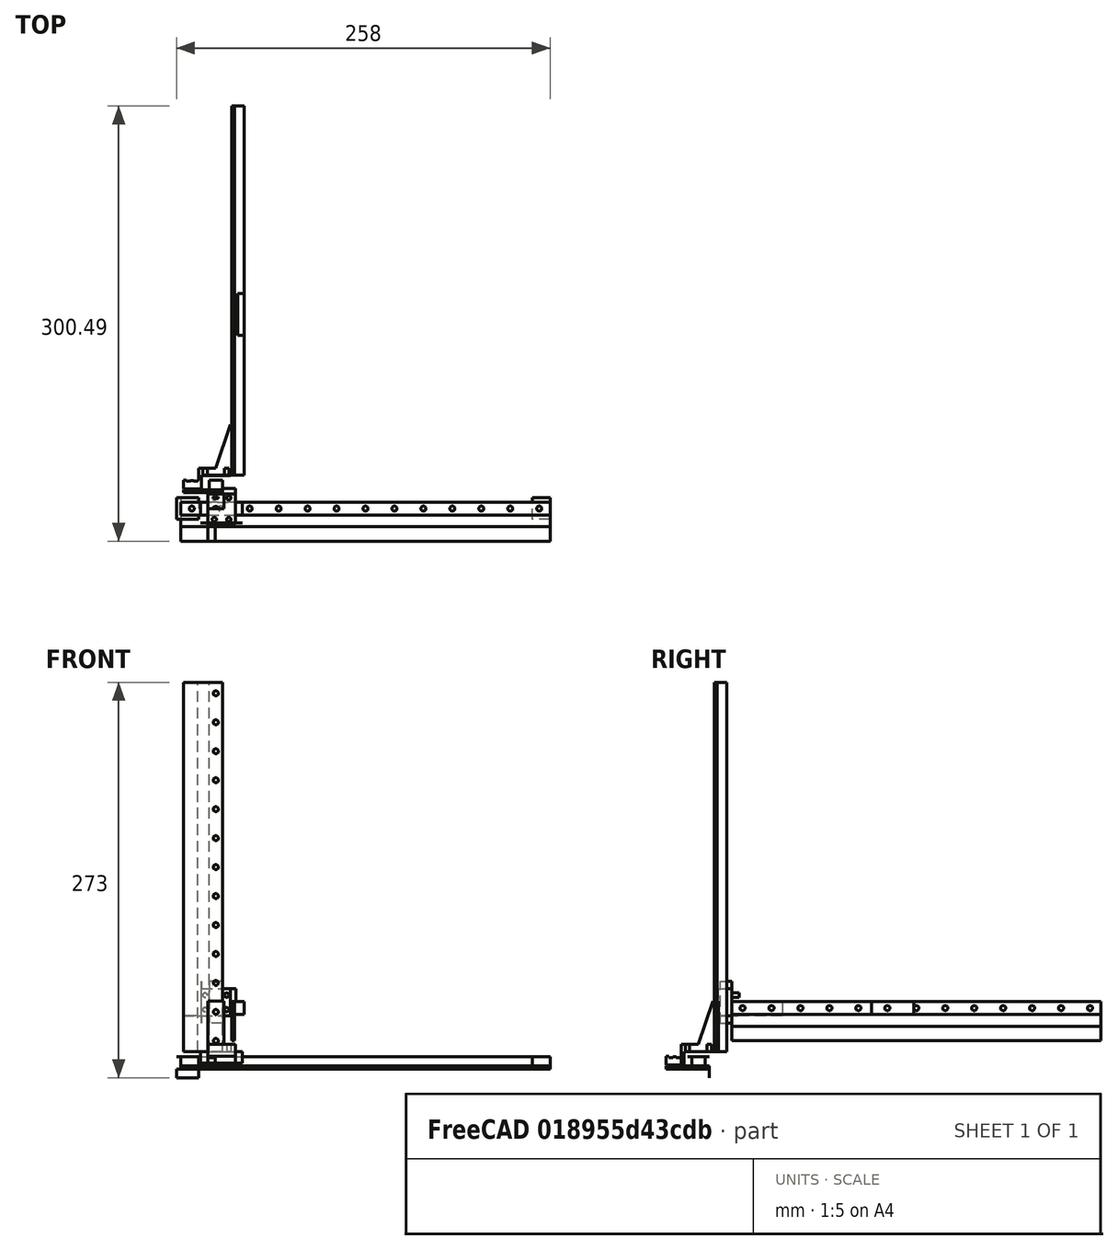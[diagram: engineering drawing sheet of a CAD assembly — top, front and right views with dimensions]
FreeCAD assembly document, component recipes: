
FREECAD ASSEMBLY — COMPONENT RECIPES ("v7")

This assembly document has 14 components, labeled P0..P13 below (a component is one placed body or linked part). 11 of them carry a construction recipe — the FreeCAD feature program that regenerates the part from scratch, quoted from this document or its linked companion documents; the rest are supplied as boundary geometry only. No exploded tour is included for this assembly.
COMPONENT P0 — recipe-attached ("Base_PCBLB", a linked part whose construction recipe lives in a companion FreeCAD document of the same project; that document's serialized recipe follows).
Construction recipe (the companion document, serialized — sketch geometry with constraints, then the solid features built on it; lengths are millimeters unless a unit is written):

FCSTD DOCUMENT  (FreeCAD 0.21R33668 +26 (Git))
Label: Base
License: All rights reserved
LicenseURL: http://en.wikipedia.org/wiki/All_rights_reserved
objects: Sketcher::SketchObject×4, PartDesign::Pad×3, PartDesign::SubShapeBinder×2, PartDesign::Pocket×1, PartDesign::Body×1
note: 15 computed .brp shape members not serialized (recipe doc carries the construction recipe); baked Part::Feature solids carry a one-line shape summary decoded from their .brp
EXTERNAL_REF file=MG/mgn9c_13.FCStd obj=Body
EXTERNAL_REF file=MG/mgn9c_slide.FCStd obj=Body001
EXTERNAL_REF file=MG/Datasheet.FCStd obj=Spreadsheet

FEATURE [PartDesign::SubShapeBinder] Binder  label="Rail"
  BindCopyOnChange = 0
  BindMode = 0
  ClaimChildren = false
  Context = -> Body [Binder.]
  Fuse = false
  MakeFace = true
  OffsetFill = false
  OffsetIntersection = false
  OffsetJoinType = 0
  OffsetOpenResult = false
  PartialLoad = false
  Relative = true
  Support = -> [<external MG/mgn9c_13.FCStd>#Body[LinearPattern.]]
  _Version = 2
FEATURE [PartDesign::SubShapeBinder] Binder001  label="Slide"
  BindCopyOnChange = 0
  BindMode = 0
  ClaimChildren = false
  Context = -> Body [Binder001.]
  Fuse = false
  MakeFace = true
  OffsetFill = false
  OffsetIntersection = false
  OffsetJoinType = 0
  OffsetOpenResult = false
  PartialLoad = false
  Placement = pos=(12,-5.5,2) rot=(0,0,1;0rad)
  Relative = true
  Support = -> [<external MG/mgn9c_slide.FCStd>#Body001]
  _Version = 2
FEATURE [Sketcher::SketchObject] Sketch
  ExternalGeometry = -> [Binder]
  FullyConstrained = true
  MapMode = 5
  Support = -> [XY_Plane]
  expr: Constraints[22] = .Constraints.Strength
  expr: Constraints[30] = .Constraints.Strength
  sketch-geometry (13):
    g0: LineSegment StartX=0 StartY=9 StartZ=0 EndX=12.25 EndY=9 EndZ=0
    g1: LineSegment StartX=12.25 StartY=0 StartZ=0 EndX=0 EndY=0 EndZ=0
    g2: LineSegment StartX=0 StartY=0 StartZ=0 EndX=0 EndY=9 EndZ=0
    g3: LineSegment StartX=12.25 StartY=-3 StartZ=0 EndX=-3 EndY=-3 EndZ=0
    g4: LineSegment StartX=-3 StartY=-3 StartZ=0 EndX=-3 EndY=12 EndZ=0
    g5: LineSegment StartX=-3 StartY=12 StartZ=0 EndX=12.25 EndY=12 EndZ=0
    g6: LineSegment StartX=12.25 StartY=12 StartZ=0 EndX=12.25 EndY=-3 EndZ=0
    g7: LineSegment StartX=12.25 StartY=12 StartZ=0 EndX=12.25 EndY=9 EndZ=0
    g8: LineSegment StartX=12.25 StartY=-3 StartZ=0 EndX=12.25 EndY=0 EndZ=0
    g9: GeomPoint X=12.25 Y=4.5 Z=0
    g10: LineSegment StartX=0 StartY=4.5 StartZ=0 EndX=12.25 EndY=4.5 EndZ=0
    g11: GeomPoint X=9.25 Y=4.5 Z=0
    g12: LineSegment StartX=0 StartY=0 StartZ=0 EndX=12.25 EndY=0 EndZ=0
  constraints (34):
    c: Coincident(g1,g2)
    c: Coincident(g2,g0)
    c: Horizontal(g0)
    c: Horizontal(g1)
    c: Vertical(g2)
    c: Coincident(g0,g-3)
    c: PointOnObject(g1,g-4)
    c: Coincident(g3,g4)
    c: Coincident(g4,g5)
    c: Coincident(g5,g6)
    c: Coincident(g6,g3)
    c: Horizontal(g3)
    c: Horizontal(g5)
    c: Vertical(g4)
    c: Vertical(g6)
    c: PointOnObject(g0,g6)
    c: Coincident(g7,g5)
    c: Coincident(g7,g0)
    c: Coincident(g8,g3)
    c: Coincident(g8,g1)
    c: Vertical(g8)
    c: DistanceY(g8,g8) = 3  'Strength'
    c: DistanceX(g3,g1) = 3
    c: PointOnObject(g9,g6)
    c: PointOnObject(g10,g2)
    c: Coincident(g10,g9)
    c: PointOnObject(g-5,g10)
    c: Symmetric(g3,g5,g10)
    c: PointOnObject(g11,g-5)
    c: PointOnObject(g11,g10)
    c: DistanceX(g11,g9) = 3
    c: Coincident(g12,g2)
    c: Coincident(g12,g8)
    c: DistanceX(g0,g0) = 12.25  'RailOverlap'
FEATURE [PartDesign::Pad] Pad
  Direction = (0,0,1)
  Length = 6.5
  Length2 = 10
  Profile = -> Sketch
  ReferenceAxis = -> Sketch [N_Axis]
  Type = 0
  expr: Length = <<Datasheet>>#<<mgn9c>>.Dim_Hr
FEATURE [Sketcher::SketchObject] Sketch001
  ExternalGeometry = -> [Pad]
  FullyConstrained = true
  MapMode = 5
  Placement = pos=(-3,0,0) rot=(0.57735,-0.57735,-0.57735;2.0944rad)
  Support = -> [Pad]
  sketch-geometry (4):
    g0: LineSegment StartX=-12 StartY=0 StartZ=0 EndX=3 EndY=0 EndZ=0
    g1: LineSegment StartX=3 StartY=0 StartZ=0 EndX=3 EndY=-2 EndZ=0
    g2: LineSegment StartX=3 StartY=-2 StartZ=0 EndX=-12 EndY=-2 EndZ=0
    g3: LineSegment StartX=-12 StartY=-2 StartZ=0 EndX=-12 EndY=0 EndZ=0
  constraints (10):
    c: Coincident(g0,g1)
    c: Coincident(g1,g2)
    c: Coincident(g2,g3)
    c: Coincident(g3,g0)
    c: Horizontal(g2)
    c: Vertical(g1)
    c: Vertical(g3)
    c: Coincident(g0,g-4)
    c: Coincident(g0,g-4)
    c: DistanceY(g1,g1) = 2  'PCB_Thickness'
FEATURE [PartDesign::Pad] Pad001
  BaseFeature = -> Pad
  Direction = (-1,0,0)
  Length = 3
  Length2 = 10
  Profile = -> Sketch001
  ReferenceAxis = -> Sketch001 [N_Axis]
  Reversed = true
  Type = 0
  expr: Length = <<Sketch>>.Constraints.Strength
FEATURE [Sketcher::SketchObject] Sketch002
  ExternalGeometry = -> [Pad001,Binder]
  FullyConstrained = true
  MapMode = 5
  Placement = pos=(0,0,-2) rot=(1,0,0;3.14159rad)
  Support = -> [Pad001]
  sketch-geometry (5):
    g0: LineSegment StartX=-3 StartY=-12 StartZ=0 EndX=12.25 EndY=-12 EndZ=0
    g1: LineSegment StartX=12.25 StartY=-12 StartZ=0 EndX=12.25 EndY=3 EndZ=0
    g2: LineSegment StartX=12.25 StartY=3 StartZ=0 EndX=-3 EndY=3 EndZ=0
    g3: LineSegment StartX=-3 StartY=3 StartZ=0 EndX=-3 EndY=-12 EndZ=0
    g4: Circle CenterX=7.5 CenterY=-4.5 CenterZ=0 NormalX=0 NormalY=0 NormalZ=1 AngleXU=0 Radius=1.75
  constraints (12):
    c: Coincident(g0,g1)
    c: Coincident(g1,g2)
    c: Coincident(g2,g3)
    c: Coincident(g3,g0)
    c: Horizontal(g0)
    c: Horizontal(g2)
    c: Vertical(g1)
    c: Vertical(g3)
    c: Coincident(g0,g-5)
    c: Coincident(g1,g-4)
    c: Coincident(g4,g-7)
    c: PointOnObject(g-6,g4)
FEATURE [PartDesign::Pad] Pad002
  BaseFeature = -> Pad001
  Direction = (0,0,-1)
  Length = 6
  Length2 = 10
  Profile = -> Sketch002
  ReferenceAxis = -> Sketch002 [N_Axis]
  Type = 0
  expr: Length = 6
FEATURE [Sketcher::SketchObject] Sketch003
  ExternalGeometry = -> [Pad002]
  FullyConstrained = true
  MapMode = 5
  Placement = pos=(0,0,-8) rot=(1,0,0;3.14159rad)
  Support = -> [Pad002]
  expr: Constraints[1] = <<Datasheet>>#<<mgn9c>>.Dim_D
  sketch-geometry (1):
    g0: Circle CenterX=7.5 CenterY=-4.5 CenterZ=0 NormalX=0 NormalY=0 NormalZ=1 AngleXU=0 Radius=3
  constraints (2):
    c: Coincident(g0,g-3)
    c: Diameter(g0) = 6
FEATURE [PartDesign::Pocket] Pocket
  BaseFeature = -> Pad002
  Direction = (0,0,1)
  Length = 5
  Length2 = 5
  Profile = -> Sketch003
  ReferenceAxis = -> Sketch003 [N_Axis]
  Type = 0
FEATURE [PartDesign::Body] Body  label="Base_PCB"
  Group = -> [Sketch,Binder001,Binder,Pad,Sketch001,Pad001,Sketch002,Pad002,Sketch003,Pocket]
  Origin = -> Origin
  Tip = -> Pocket
COMPONENT P1 — recipe-attached ("PCB", a linked part whose construction recipe lives in a companion FreeCAD document of the same project; that document's serialized recipe follows).
Construction recipe (the companion document, serialized — sketch geometry with constraints, then the solid features built on it; lengths are millimeters unless a unit is written):

FCSTD DOCUMENT  (FreeCAD 0.21R33668 +26 (Git))
Label: PCB_Linear_Potentiometer
License: All rights reserved
LicenseURL: http://en.wikipedia.org/wiki/All_rights_reserved
objects: Sketcher::SketchObject×3, PartDesign::SubShapeBinder×2, PartDesign::Pad×2, PartDesign::Pocket×1, PartDesign::LinearPattern×1, PartDesign::Body×1
note: 13 computed .brp shape members not serialized (recipe doc carries the construction recipe); baked Part::Feature solids carry a one-line shape summary decoded from their .brp
EXTERNAL_REF file=MG/mgn9c_13.FCStd obj=Body
EXTERNAL_REF file=MG/mgn9c_slide.FCStd obj=Body001
EXTERNAL_REF file=MG/Datasheet.FCStd obj=Spreadsheet
EXTERNAL_REF file=NormalConnector.FCStd obj=Sketch
EXTERNAL_REF file=Base.FCStd obj=Sketch001
EXTERNAL_REF file=Base.FCStd obj=Sketch

FEATURE [PartDesign::SubShapeBinder] Binder  label="Rail"
  BindCopyOnChange = 0
  BindMode = 0
  ClaimChildren = false
  Context = -> Body [Binder.]
  Fuse = false
  MakeFace = true
  OffsetFill = false
  OffsetIntersection = false
  OffsetJoinType = 0
  OffsetOpenResult = false
  PartialLoad = false
  Relative = true
  Support = -> [<external MG/mgn9c_13.FCStd>#Body]
  _Version = 2
FEATURE [PartDesign::SubShapeBinder] Binder001  label="Slide"
  BindCopyOnChange = 0
  BindMode = 0
  ClaimChildren = false
  Context = -> Body [Binder001.]
  Fuse = false
  MakeFace = true
  OffsetFill = false
  OffsetIntersection = false
  OffsetJoinType = 0
  OffsetOpenResult = false
  PartialLoad = false
  Placement = pos=(0,-5.5,0) rot=(0,0,1;0rad)
  Relative = true
  Support = -> [<external MG/mgn9c_slide.FCStd>#Body001]
  _Version = 2
FEATURE [Sketcher::SketchObject] Sketch
  ExternalGeometry = -> [Binder]
  FullyConstrained = true
  MapMode = 5
  Support = -> [XY_Plane]
  expr: Constraints[21] = <<Datasheet>>#<<mgn9c>>.Dim_W
  expr: Constraints[22] = NormalConnector#Sketch.Constraints.PCB_Edge_Distance_From_Slide_Side
  sketch-geometry (11):
    g0: LineSegment StartX=0 StartY=9 StartZ=0 EndX=255 EndY=9 EndZ=0
    g1: LineSegment StartX=255 StartY=9 StartZ=0 EndX=255 EndY=-17.9944 EndZ=0
    g2: LineSegment StartX=255 StartY=-17.9944 StartZ=0 EndX=0 EndY=-17.9944 EndZ=0
    g3: LineSegment StartX=0 StartY=-17.9944 StartZ=0 EndX=0 EndY=9 EndZ=0
    g4: LineSegment StartX=7.5 StartY=4.5 StartZ=0 EndX=27.5 EndY=4.5 EndZ=0
    g5: LineSegment StartX=7.5 StartY=14.5 StartZ=0 EndX=27.5 EndY=14.5 EndZ=0
    g6: LineSegment StartX=27.5 StartY=14.5 StartZ=0 EndX=27.5 EndY=-5.5 EndZ=0
    g7: LineSegment StartX=27.5 StartY=-5.5 StartZ=0 EndX=7.5 EndY=-5.5 EndZ=0
    g8: LineSegment StartX=7.5 StartY=-5.5 StartZ=0 EndX=7.5 EndY=14.5 EndZ=0
    g9: Circle CenterX=7.5 CenterY=4.5 CenterZ=0 NormalX=0 NormalY=0 NormalZ=1 AngleXU=0 Radius=1.75
    g10: GeomPoint X=9.25 Y=4.5 Z=0
  constraints (29):
    c: Coincident(g0,g1)
    c: Coincident(g1,g2)
    c: Coincident(g2,g3)
    c: Coincident(g3,g0)
    c: Horizontal(g2)
    c: Vertical(g1)
    c: Vertical(g3)
    c: Coincident(g0,g-3)
    c: Coincident(g0,g-4)
    c: Coincident(g4,g-5)
    c: Coincident(g4,g-6)
    c: Coincident(g5,g6)
    c: Coincident(g6,g7)
    c: Coincident(g7,g8)
    c: Coincident(g8,g5)
    c: Horizontal(g5)
    c: Horizontal(g7)
    c: Vertical(g6)
    c: PointOnObject(g4,g6)
    c: PointOnObject(g4,g8)
    c: Symmetric(g5,g7,g4)
    c: DistanceY(g8,g8) = 20
    c: DistanceY(g2,g7) = 12.4944
    c: Coincident(g9,g4)
    c: PointOnObject(g10,g4)
    c: PointOnObject(g10,g-5)
    c: PointOnObject(g10,g9)
    c: DistanceX(g0,g0) = 255  'Length'
    c: DistanceY(g1,g1) = 26.9944
FEATURE [PartDesign::Pad] Pad
  Direction = (0,0,1)
  Length = 2
  Length2 = 10
  Profile = -> Sketch
  ReferenceAxis = -> Sketch [N_Axis]
  Type = 0
  expr: Length = <<Base>>#<<Sketch001>>.Constraints.PCB_Thickness
FEATURE [Sketcher::SketchObject] Sketch001
  ExternalGeometry = -> [Pad]
  FullyConstrained = true
  MapMode = 5
  Placement = pos=(0,0,2) rot=(0,0,1;0rad)
  Support = -> [Pad]
  sketch-geometry (2):
    g0: Circle CenterX=7.5 CenterY=4.5 CenterZ=0 NormalX=0 NormalY=0 NormalZ=1 AngleXU=0 Radius=1.75
    g1: GeomPoint X=9.25 Y=4.5 Z=0
  constraints (4):
    c: PointOnObject(g1,g0)
    c: PointOnObject(g1,g-3)
    c: Coincident(g0,g-3)
    c: DistanceY(g1,g0) = 0
FEATURE [PartDesign::Pocket] Pocket
  BaseFeature = -> Pad
  Direction = (0,0,-1)
  Length = 5
  Length2 = 5
  Profile = -> Sketch001
  ReferenceAxis = -> Sketch001 [N_Axis]
  Type = 1
FEATURE [PartDesign::LinearPattern] LinearPattern
  BaseFeature = -> Pocket
  Direction = -> Sketch001 [H_Axis]
  Length = 240
  Occurrences = 13
  Originals = -> [Pocket]
  expr: Length = <<Sketch>>.Constraints.Length - <<Datasheet>>#<<mgn9c>>.Dim_E * 2
FEATURE [Sketcher::SketchObject] Sketch002
  ExternalGeometry = -> [LinearPattern]
  FullyConstrained = true
  MapMode = 5
  Placement = pos=(0,0,2) rot=(0,0,1;0rad)
  Support = -> [LinearPattern]
  expr: Constraints[18] = <<Datasheet>>#<<mgn9c>>.Dim_W / 2
  expr: Constraints[21] = NormalConnector#Sketch.Constraints.Connector_Close_Distance
  expr: Constraints[22] = NormalConnector#Sketch.Constraints.Connector_Far_Distance
  expr: Constraints[24] = .Constraints.Resistor_Width
  expr: Constraints[26] = <<Base>>#<<Sketch>>.Constraints.RailOverlap
  sketch-geometry (15):
    g0: LineSegment StartX=12.25 StartY=-7.4986 StartZ=0 EndX=242.75 EndY=-7.4986 EndZ=0
    g1: LineSegment StartX=242.75 StartY=-7.4986 StartZ=0 EndX=242.75 EndY=-11.4986 EndZ=0
    g2: LineSegment StartX=242.75 StartY=-11.4986 StartZ=0 EndX=12.25 EndY=-11.4986 EndZ=0
    g3: LineSegment StartX=12.25 StartY=-11.4986 StartZ=0 EndX=12.25 EndY=-7.4986 EndZ=0
    g4: LineSegment StartX=12.25 StartY=-12.4958 StartZ=0 EndX=242.75 EndY=-12.4958 EndZ=0
    g5: LineSegment StartX=242.75 StartY=-12.4958 StartZ=0 EndX=242.75 EndY=-16.4958 EndZ=0
    g6: LineSegment StartX=242.75 StartY=-16.4958 StartZ=0 EndX=12.25 EndY=-16.4958 EndZ=0
    g7: LineSegment StartX=12.25 StartY=-16.4958 StartZ=0 EndX=12.25 EndY=-12.4958 EndZ=0
    g8: GeomPoint X=12.25 Y=-9.4986 Z=0
    g9: GeomPoint X=12.25 Y=-14.4958 Z=0
    g10: GeomPoint X=0 Y=4.5 Z=0
    g11: GeomPoint X=0 Y=-5.5 Z=0
    g12: GeomPoint X=12.25 Y=9 Z=0
    g13: GeomPoint X=242.75 Y=9 Z=0
    g14: GeomPoint X=127.5 Y=9 Z=0
  constraints (33):
    c: Coincident(g0,g1)
    c: Coincident(g1,g2)
    c: Coincident(g2,g3)
    c: Coincident(g3,g0)
    c: Horizontal(g0)
    c: Horizontal(g2)
    c: Vertical(g1)
    c: Vertical(g3)
    c: Coincident(g4,g5)
    c: Coincident(g5,g6)
    c: Coincident(g6,g7)
    c: Coincident(g7,g4)
    c: Horizontal(g4)
    c: Horizontal(g6)
    c: Vertical(g5)
    c: Vertical(g7)
    c: Symmetric(g-4,g-1,g10)
    c: PointOnObject(g11,g-4)
    c: DistanceY(g11,g10) = 10
    c: Symmetric(g2,g0,g8)
    c: Symmetric(g4,g6,g9)
    c: DistanceY(g8,g11) = 3.9986
    c: DistanceY(g9,g11) = 8.9958
    c: DistanceY(g3,g3) = 4  'Resistor_Width'
    c: DistanceY(g7,g7) = 4
    c: PointOnObject(g12,g-7)
    c: DistanceX(g-7,g12) = 12.25
    c: Vertical(g8,g9)
    c: Vertical(g12,g8)
    c: Symmetric(g13,g12,g14)
    c: Symmetric(g-7,g-7,g14)
    c: Vertical(g0,g13)
    c: Vertical(g4,g1)
FEATURE [PartDesign::Pad] Pad001
  BaseFeature = -> LinearPattern
  Direction = (0,0,1)
  Length = 0.1
  Length2 = 10
  Profile = -> Sketch002
  ReferenceAxis = -> Sketch002 [N_Axis]
  Type = 0
FEATURE [PartDesign::Body] Body  label="PCB"
  Group = -> [Binder,Binder001,Sketch,Pad,Sketch001,Pocket,LinearPattern,Sketch002,Pad001]
  Origin = -> Origin
  Tip = -> Pad001
COMPONENT P2 — geometry summary ("RailXL"; no construction recipe available for this part):
  bounding box: 255.0 x 9.0 x 6.5 mm
  tessellated surface: 3,548 triangles
  volume: 14105 mm^3 (95% of its bounding box)
  symmetry: 2-fold rotationally symmetric about the x axis; 2-fold rotationally symmetric about the y axis; 2-fold rotationally symmetric about the z axis; mirror-symmetric across its x mid-plane, y mid-plane, z mid-plane
COMPONENT P3 — same part as P0; its construction recipe is shown at P0.
COMPONENT P4 — recipe-attached ("Slide", a linked part whose construction recipe lives in a companion FreeCAD document of the same project; that document's serialized recipe follows).
Construction recipe (the companion document, serialized — sketch geometry with constraints, then the solid features built on it; lengths are millimeters unless a unit is written):

FCSTD DOCUMENT  (FreeCAD 0.21R33668 +26 (Git))
Label: mgn9c_slide
License: All rights reserved
LicenseURL: http://en.wikipedia.org/wiki/All_rights_reserved
objects: Sketcher::SketchObject×4, PartDesign::Pocket×3, App::Link×1, PartDesign::Pad×1, PartDesign::Body×1
note: 13 computed .brp shape members not serialized (recipe doc carries the construction recipe); baked Part::Feature solids carry a one-line shape summary decoded from their .brp
EXTERNAL_REF file=Datasheet.FCStd obj=Spreadsheet

FEATURE [App::Link] Link  label="mgn9c"
  LinkedObject = -> <external Datasheet.FCStd>#Spreadsheet
FEATURE [Sketcher::SketchObject] Sketch002
  FullyConstrained = true
  MapMode = 5
  Support = -> [XY_Plane001]
  expr: Constraints[10] = <<mgn9c>>.Dim_W
  expr: Constraints[9] = <<mgn9c>>.Dim_L
  sketch-geometry (4):
    g0: LineSegment StartX=0 StartY=0 StartZ=0 EndX=28.9 EndY=0 EndZ=0
    g1: LineSegment StartX=28.9 StartY=0 StartZ=0 EndX=28.9 EndY=20 EndZ=0
    g2: LineSegment StartX=28.9 StartY=20 StartZ=0 EndX=0 EndY=20 EndZ=0
    g3: LineSegment StartX=0 StartY=20 StartZ=0 EndX=0 EndY=0 EndZ=0
  constraints (11):
    c: Coincident(g0,g1)
    c: Coincident(g1,g2)
    c: Coincident(g2,g3)
    c: Coincident(g3,g0)
    c: Horizontal(g0)
    c: Horizontal(g2)
    c: Vertical(g1)
    c: Vertical(g3)
    c: Coincident(g0,g-1)
    c: DistanceX(g2,g2) = 28.9
    c: DistanceY(g1,g1) = 20
FEATURE [PartDesign::Pad] Pad001
  Direction = (0,0,1)
  Length = 8
  Length2 = 10
  Profile = -> Sketch002
  ReferenceAxis = -> Sketch002 [N_Axis]
  Type = 0
  expr: Length = <<mgn9c>>.Dim_H - <<mgn9c>>.Dim_H1
FEATURE [Sketcher::SketchObject] Sketch003
  ExternalGeometry = -> [Pad001]
  FullyConstrained = true
  MapMode = 5
  Placement = pos=(0,0,0) rot=(0.57735,-0.57735,-0.57735;2.0944rad)
  Support = -> [Pad001]
  expr: Constraints[10] = <<mgn9c>>.Dim_Hr - <<mgn9c>>.Dim_H1
  expr: Constraints[8] = <<mgn9c>>.Dim_N
  expr: Constraints[9] = <<mgn9c>>.Dim_N
  sketch-geometry (4):
    g0: LineSegment StartX=-14.5 StartY=0 StartZ=0 EndX=-5.5 EndY=0 EndZ=0
    g1: LineSegment StartX=-5.5 StartY=0 StartZ=0 EndX=-5.5 EndY=4.5 EndZ=0
    g2: LineSegment StartX=-5.5 StartY=4.5 StartZ=0 EndX=-14.5 EndY=4.5 EndZ=0
    g3: LineSegment StartX=-14.5 StartY=4.5 StartZ=0 EndX=-14.5 EndY=0 EndZ=0
  constraints (12):
    c: Coincident(g0,g1)
    c: Coincident(g1,g2)
    c: Coincident(g2,g3)
    c: Coincident(g3,g0)
    c: Horizontal(g0)
    c: Horizontal(g2)
    c: Vertical(g1)
    c: Vertical(g3)
    c: DistanceX(g-5,g0) = 5.5
    c: DistanceX(g0,g-6) = 5.5
    c: DistanceY(g1,g1) = 4.5
    c: PointOnObject(g0,g-5)
FEATURE [PartDesign::Pocket] Pocket001
  BaseFeature = -> Pad001
  Direction = (1,0,0)
  Length = 28.9
  Length2 = 5
  Profile = -> Sketch003
  ReferenceAxis = -> Sketch003 [N_Axis]
  Type = 0
  expr: Length = <<mgn9c>>.Dim_L
FEATURE [Sketcher::SketchObject] Sketch004
  ExternalGeometry = -> [Pocket001]
  FullyConstrained = true
  MapMode = 5
  Placement = pos=(0,0,8) rot=(0,0,1;0rad)
  Support = -> [Pocket001]
  expr: Constraints[17] = 3
  expr: Constraints[18] = 3
  expr: Constraints[19] = 3
  expr: Constraints[20] = 3
  expr: Constraints[8] = <<mgn9c>>.Dim_C
  expr: Constraints[9] = <<mgn9c>>.Dim_B
  sketch-geometry (9):
    g0: LineSegment StartX=9.45 StartY=17.5 StartZ=0 EndX=19.45 EndY=17.5 EndZ=0
    g1: LineSegment StartX=19.45 StartY=17.5 StartZ=0 EndX=19.45 EndY=2.5 EndZ=0
    g2: LineSegment StartX=19.45 StartY=2.5 StartZ=0 EndX=9.45 EndY=2.5 EndZ=0
    g3: LineSegment StartX=9.45 StartY=2.5 StartZ=0 EndX=9.45 EndY=17.5 EndZ=0
    g4: GeomPoint X=14.45 Y=10 Z=0
    g5: Circle CenterX=9.45 CenterY=17.5 CenterZ=0 NormalX=0 NormalY=0 NormalZ=1 AngleXU=0 Radius=1.5
    g6: Circle CenterX=19.45 CenterY=17.5 CenterZ=0 NormalX=0 NormalY=0 NormalZ=1 AngleXU=0 Radius=1.5
    g7: Circle CenterX=19.45 CenterY=2.5 CenterZ=0 NormalX=0 NormalY=0 NormalZ=1 AngleXU=0 Radius=1.5
    g8: Circle CenterX=9.45 CenterY=2.5 CenterZ=0 NormalX=0 NormalY=0 NormalZ=1 AngleXU=0 Radius=1.5
  constraints (21):
    c: Coincident(g0,g1)
    c: Coincident(g1,g2)
    c: Coincident(g2,g3)
    c: Coincident(g3,g0)
    c: Horizontal(g0)
    c: Horizontal(g2)
    c: Vertical(g1)
    c: Vertical(g3)
    c: DistanceX(g0,g0) = 10
    c: DistanceY(g1,g1) = 15
    c: DistanceY(g-4,g2) = 2.5
    c: Symmetric(g-3,g-4,g4)
    c: Symmetric(g1,g0,g4)
    c: Coincident(g5,g0)
    c: Coincident(g6,g0)
    c: Coincident(g7,g1)
    c: Coincident(g8,g2)
    c: Diameter(g8) = 3
    c: Diameter(g7) = 3
    c: Diameter(g6) = 3
    c: Diameter(g5) = 3
FEATURE [PartDesign::Pocket] Pocket002
  BaseFeature = -> Pocket001
  Direction = (0,0,-1)
  Length = 3
  Length2 = 5
  Profile = -> Sketch004
  ReferenceAxis = -> Sketch004 [N_Axis]
  Type = 0
FEATURE [Sketcher::SketchObject] Sketch005
  ExternalGeometry = -> [Pocket002]
  FullyConstrained = true
  MapMode = 5
  Placement = pos=(0,0,8) rot=(0,0,1;0rad)
  Support = -> [Pocket002]
  expr: Constraints[19] = <<mgn9c>>.Dim_L1
  sketch-geometry (9):
    g0: LineSegment StartX=0 StartY=20 StartZ=0 EndX=5 EndY=20 EndZ=0
    g1: LineSegment StartX=5 StartY=20 StartZ=0 EndX=5 EndY=0 EndZ=0
    g2: LineSegment StartX=5 StartY=0 StartZ=0 EndX=0 EndY=0 EndZ=0
    g3: LineSegment StartX=0 StartY=0 StartZ=0 EndX=0 EndY=20 EndZ=0
    g4: LineSegment StartX=28.9 StartY=0 StartZ=0 EndX=23.9 EndY=0 EndZ=0
    g5: LineSegment StartX=23.9 StartY=0 StartZ=0 EndX=23.9 EndY=20 EndZ=0
    g6: LineSegment StartX=23.9 StartY=20 StartZ=0 EndX=28.9 EndY=20 EndZ=0
    g7: LineSegment StartX=28.9 StartY=20 StartZ=0 EndX=28.9 EndY=0 EndZ=0
    g8: GeomPoint X=14.45 Y=0 Z=0
  constraints (22):
    c: Coincident(g0,g1)
    c: Coincident(g1,g2)
    c: Coincident(g2,g3)
    c: Coincident(g3,g0)
    c: Horizontal(g0)
    c: Horizontal(g2)
    c: Vertical(g1)
    c: Vertical(g3)
    c: Coincident(g0,g-3)
    c: PointOnObject(g1,g-1)
    c: Coincident(g4,g5)
    c: Coincident(g5,g6)
    c: Coincident(g6,g7)
    c: Coincident(g7,g4)
    c: Horizontal(g6)
    c: Vertical(g5)
    c: Vertical(g7)
    c: Symmetric(g2,g-4,g8)
    c: Symmetric(g4,g1,g8)
    c: DistanceX(g1,g4) = 18.9
    c: PointOnObject(g5,g-5)
    c: Coincident(g4,g-4)
FEATURE [PartDesign::Pocket] Pocket003
  BaseFeature = -> Pocket002
  Direction = (0,0,-1)
  Length = 0.1
  Length2 = 5
  Profile = -> Sketch005
  ReferenceAxis = -> Sketch005 [N_Axis]
  Type = 0
FEATURE [PartDesign::Body] Body001  label="Slide"
  Group = -> [Sketch002,Pad001,Sketch003,Pocket001,Sketch004,Pocket002,Sketch005,Pocket003]
  Origin = -> Origin001
  Tip = -> Pocket003
COMPONENT P5 — recipe-attached ("NormalConnector", a linked part whose construction recipe lives in a companion FreeCAD document of the same project; that document's serialized recipe follows).
Construction recipe (the companion document, serialized — sketch geometry with constraints, then the solid features built on it; lengths are millimeters unless a unit is written):

FCSTD DOCUMENT  (FreeCAD 0.21R33668 +26 (Git))
Label: NormalConnector
License: All rights reserved
LicenseURL: http://en.wikipedia.org/wiki/All_rights_reserved
objects: Sketcher::SketchObject×7, PartDesign::Pocket×6, PartDesign::SubShapeBinder×4, PartDesign::Pad×1, PartDesign::Body×1
note: 26 computed .brp shape members not serialized (recipe doc carries the construction recipe); baked Part::Feature solids carry a one-line shape summary decoded from their .brp
EXTERNAL_REF file=MG/mgn9c_slide.FCStd obj=Body001
EXTERNAL_REF file=Base.FCStd obj=Sketch001
EXTERNAL_REF file=MG/Datasheet.FCStd obj=Spreadsheet
EXTERNAL_REF file=MG/mgn9c_13.FCStd obj=Body
EXTERNAL_REF file=OmniballConnector/OmniballConnector_7945.FCStd obj=Sketch002
EXTERNAL_REF file=OmniballConnector/OmniballConnector_7945.FCStd obj=Body

FEATURE [PartDesign::SubShapeBinder] Binder  label="Slide"
  BindCopyOnChange = 0
  BindMode = 0
  ClaimChildren = false
  Context = -> Body [Binder.]
  Fuse = false
  MakeFace = true
  OffsetFill = false
  OffsetIntersection = false
  OffsetJoinType = 0
  OffsetOpenResult = false
  PartialLoad = false
  Placement = pos=(-5,0,-2) rot=(0,0,1;0rad)
  Relative = true
  Support = -> [<external MG/mgn9c_slide.FCStd>#Body001]
  _Version = 2
FEATURE [PartDesign::SubShapeBinder] Binder001  label="Rail"
  BindCopyOnChange = 0
  BindMode = 0
  ClaimChildren = false
  Context = -> Body [Binder001.]
  Fuse = false
  MakeFace = true
  OffsetFill = false
  OffsetIntersection = false
  OffsetJoinType = 0
  OffsetOpenResult = false
  PartialLoad = false
  Placement = pos=(-5,5.5,-2) rot=(0,0,1;0rad)
  Relative = true
  Support = -> [<external MG/mgn9c_13.FCStd>#Body]
  _Version = 2
FEATURE [Sketcher::SketchObject] Sketch
  ExternalGeometry = -> [Binder,Binder001]
  FullyConstrained = true
  MapMode = 5
  Placement = pos=(0,0,0) rot=(0.57735,0.57735,0.57735;2.0944rad)
  Support = -> [YZ_Plane]
  expr: Constraints[108] = <<Datasheet>>#<<mgn9c>>.Dim_H1
  expr: Constraints[11] = 0.102 in
  expr: Constraints[20] = 0.118 in
  expr: Constraints[23] = 0.03 in
  expr: Constraints[24] = 0.236 in
  expr: Constraints[25] = 0.091 in
  expr: Constraints[27] = 0.266 in
  expr: Constraints[88] = <<Datasheet>>#<<mgn9c>>.Dim_E * 2 + <<Datasheet>>#<<mgn9c>>.Dim_P
  expr: Constraints[98] = 2 mm + <<Base>>#<<Sketch001>>.Constraints.PCB_Thickness
  sketch-geometry (44):
    g0: LineSegment StartX=2.9e-15 StartY=6 StartZ=0 EndX=2.9e-15 EndY=-4 EndZ=0
    g1: LineSegment StartX=14.5 StartY=-2 StartZ=0 EndX=-25.5 EndY=-2 EndZ=0
    g2: LineSegment StartX=-5.294 StartY=1.9944 StartZ=0 EndX=-2.7032 EndY=1.9944 EndZ=0
    g3: LineSegment StartX=-2.7032 StartY=1.9944 StartZ=0 EndX=-2.7032 EndY=-3.238 EndZ=0
    g4: LineSegment StartX=-2.7032 StartY=-3.238 StartZ=0 EndX=-5.294 EndY=-3.238 EndZ=0
    g5: LineSegment StartX=-5.294 StartY=-3.238 StartZ=0 EndX=-5.294 EndY=1.9944 EndZ=0
    g6: LineSegment StartX=-5.4972 StartY=2.7564 StartZ=0 EndX=-2.5 EndY=2.7564 EndZ=0
    g7: LineSegment StartX=-2.5 StartY=2.7564 StartZ=0 EndX=-2.5 EndY=1.9944 EndZ=0
    g8: LineSegment StartX=-2.5 StartY=1.9944 StartZ=0 EndX=-5.4972 EndY=1.9944 EndZ=0
    g9: LineSegment StartX=-5.4972 StartY=1.9944 StartZ=0 EndX=-5.4972 EndY=2.7564 EndZ=0
    g10: GeomPoint X=-3.9986 Y=1.9944 Z=0
    g11: Circle CenterX=-3.9986 CenterY=-2.8443 CenterZ=0 NormalX=0 NormalY=0 NormalZ=1 AngleXU=0 Radius=1.1557
    g12: GeomPoint X=-3.9986 Y=-4 Z=0
    g13: LineSegment StartX=-10.2912 StartY=1.9944 StartZ=0 EndX=-7.7004 EndY=1.9944 EndZ=0
    g14: LineSegment StartX=-7.7004 StartY=1.9944 StartZ=0 EndX=-7.7004 EndY=-3.238 EndZ=0
    g15: LineSegment StartX=-7.7004 StartY=-3.238 StartZ=0 EndX=-10.2912 EndY=-3.238 EndZ=0
    g16: LineSegment StartX=-10.2912 StartY=-3.238 StartZ=0 EndX=-10.2912 EndY=1.9944 EndZ=0
    g17: LineSegment StartX=-10.4944 StartY=2.7564 StartZ=0 EndX=-7.4972 EndY=2.7564 EndZ=0
    g18: LineSegment StartX=-7.4972 StartY=2.7564 StartZ=0 EndX=-7.4972 EndY=1.9944 EndZ=0
    g19: LineSegment StartX=-7.4972 StartY=1.9944 StartZ=0 EndX=-10.4944 EndY=1.9944 EndZ=0
    g20: LineSegment StartX=-10.4944 StartY=1.9944 StartZ=0 EndX=-10.4944 EndY=2.7564 EndZ=0
    g21: GeomPoint X=-8.9958 Y=1.9944 Z=0
    g22: Circle CenterX=-8.9958 CenterY=-2.8443 CenterZ=0 NormalX=0 NormalY=0 NormalZ=1 AngleXU=0 Radius=1.1557
    g23: GeomPoint X=-8.9958 Y=-4 Z=0
    g24: LineSegment StartX=-2.5 StartY=2.7564 StartZ=0 EndX=-2.5 EndY=1.9944 EndZ=0
    g25: LineSegment StartX=-2.5 StartY=1.9944 StartZ=0 EndX=-5.4972 EndY=1.9944 EndZ=0
    g26: LineSegment StartX=-5.4972 StartY=1.9944 StartZ=0 EndX=-5.4972 EndY=2.3754 EndZ=0
    g27: LineSegment StartX=-5.4972 StartY=2.3754 StartZ=0 EndX=-7.4972 EndY=2.3754 EndZ=0
    g28: LineSegment StartX=-7.4972 StartY=2.3754 StartZ=0 EndX=-7.4972 EndY=1.9944 EndZ=0
    g29: LineSegment StartX=-7.4972 StartY=1.9944 StartZ=0 EndX=-10.4944 EndY=1.9944 EndZ=0
    g30: LineSegment StartX=-10.4944 StartY=1.9944 StartZ=0 EndX=-10.4944 EndY=2.7564 EndZ=0
    g31: LineSegment StartX=-10.4944 StartY=2.7564 StartZ=0 EndX=-12.4944 EndY=2.7564 EndZ=0
    g32: LineSegment StartX=-12.4944 StartY=2.7564 StartZ=0 EndX=-12.4944 EndY=-4 EndZ=0
    g33: LineSegment StartX=-2.5 StartY=2.7564 StartZ=0 EndX=-2 EndY=2.7564 EndZ=0
    g34: LineSegment StartX=-2 StartY=2.7564 StartZ=0 EndX=-2 EndY=11 EndZ=0
    g35: LineSegment StartX=2.9e-15 StartY=-4 StartZ=0 EndX=-12.4944 EndY=-4 EndZ=0
    g36: LineSegment StartX=-2 StartY=11 StartZ=0 EndX=10 EndY=11 EndZ=0
    g37: LineSegment StartX=24 StartY=6 StartZ=0 EndX=24 EndY=41 EndZ=0
    g38: LineSegment StartX=24 StartY=41 StartZ=0 EndX=20 EndY=41 EndZ=0
    g39: LineSegment StartX=20 StartY=41 StartZ=0 EndX=10 EndY=11 EndZ=0
    g40: LineSegment StartX=2.9e-15 StartY=6 StartZ=0 EndX=24 EndY=6 EndZ=0
    g41: LineSegment StartX=-12.4944 StartY=2.7564 StartZ=0 EndX=-12.4944 EndY=-3.238 EndZ=0
    g42: LineSegment StartX=-12.4944 StartY=-3.238 StartZ=0 EndX=3.6e-15 EndY=-3.238 EndZ=0
    g43: LineSegment StartX=3.6e-15 StartY=-3.238 StartZ=0 EndX=2.9e-15 EndY=6 EndZ=0
  constraints (118):
    c: Coincident(g1,g-7)
    c: Horizontal(g1)
    c: DistanceX(g1,g1) = 40
    c: Coincident(g2,g3)
    c: Coincident(g3,g4)
    c: Coincident(g4,g5)
    c: Coincident(g5,g2)
    c: Horizontal(g2)
    c: Horizontal(g4)
    c: Vertical(g3)
    c: Vertical(g5)
    c: DistanceX(g2,g2) = 2.5908
    c: Coincident(g6,g7)
    c: Coincident(g7,g8)
    c: Coincident(g8,g9)
    c: Coincident(g9,g6)
    c: Horizontal(g6)
    c: Horizontal(g8)
    c: Vertical(g7)
    c: Vertical(g9)
    c: DistanceX(g6,g6) = 2.9972
    c: Symmetric(g8,g7,g10)
    c: Symmetric(g2,g2,g10)
    c: DistanceY(g7,g7) = 0.762
    c: DistanceY(g3,g6) = 5.9944
    c: Diameter(g11) = 2.3114
    c: DistanceX(g10,g12) = 0
    c: DistanceY(g12,g6) = 6.7564
    c: DistanceX(g11,g12) = 0
    c: Coincident(g13,g14)
    c: Coincident(g14,g15)
    c: Coincident(g15,g16)
    c: Coincident(g16,g13)
    c: Horizontal(g13)
    c: Horizontal(g15)
    c: Vertical(g14)
    c: Vertical(g16)
    c: Equal(g2,g13) = 2.5908
    c: Coincident(g17,g18)
    c: Coincident(g18,g19)
    c: Coincident(g19,g20)
    c: Coincident(g20,g17)
    c: Horizontal(g17)
    c: Horizontal(g19)
    c: Vertical(g18)
    c: Vertical(g20)
    c: Equal(g6,g17) = 2.9972
    c: Symmetric(g19,g18,g21)
    c: Symmetric(g13,g13,g21)
    c: Equal(g7,g18) = 0.762
    c: DistanceY(g14,g17) = 5.9944
    c: Equal(g11,g22) = 2.3114
    c: DistanceX(g21,g23) = 0
    c: DistanceY(g23,g17) = 6.7564
    c: DistanceX(g22,g23) = 0
    c: Coincident(g24,g6)
    c: Coincident(g24,g7)
    c: Coincident(g25,g24)
    c: Coincident(g25,g8)
    c: Coincident(g26,g25)
    c: Coincident(g27,g26)
    c: PointOnObject(g27,g18)
    c: Coincident(g28,g27)
    c: Coincident(g28,g18)
    c: Coincident(g29,g28)
    c: Coincident(g29,g19)
    c: Horizontal(g27)
    c: Symmetric(g6,g25,g26)
    c: Coincident(g30,g29)
    c: Coincident(g30,g17)
    c: Coincident(g31,g17)
    c: Horizontal(g31)
    c: DistanceX(g31,g31) = 2
    c: Coincident(g32,g31)
    c: Vertical(g32)
    c: DistanceX(g27,g27) = 2
    c: Coincident(g33,g24)
    c: DistanceX(g33,g33) = 0.5
    c: Horizontal(g33)
    c: Coincident(g34,g33)
    c: Vertical(g34)
    c: DistanceX(g33,g-5) = 2
    c: Coincident(g35,g32)
    c: Horizontal(g35)
    c: DistanceY(g0,g34) = 5
    c: Coincident(g36,g34)
    c: Horizontal(g36)
    c: Vertical(g37)
    c: DistanceY(g37,g37) = 35
    c: Coincident(g38,g37)
    c: Horizontal(g38)
    c: Coincident(g39,g38)
    c: Coincident(g36,g39)
    c: DistanceX(g36,g36) = 12
    c: Coincident(g40,g37)
    c: Horizontal(g40)
    c: Coincident(g0,g40)
    c: Coincident(g0,g-4)
    c: DistanceX(g-4,g37) = 4
    c: DistanceX(g35,g35) = 12.4944  'PCB_Edge_Distance_From_Slide_Side'
    c: DistanceX(g12,g0) = 3.9986  'Connector_Close_Distance'
    c: DistanceX(g23,g0) = 8.9958  'Connector_Far_Distance'
    c: PointOnObject(g38,g-6)
    c: Coincident(g0,g35)
    c: Vertical(g0)
    c: PointOnObject(g12,g35)
    c: PointOnObject(g12,g11)
    c: PointOnObject(g23,g35)
    c: DistanceY(g0,g-5) = 2
    c: PointOnObject(g23,g22)
    c: Coincident(g41,g31)
    c: Coincident(g42,g41)
    c: PointOnObject(g42,g0)
    c: Horizontal(g42)
    c: Coincident(g43,g42)
    c: Coincident(g43,g40)
    c: PointOnObject(g3,g42)
    c: PointOnObject(g41,g32)
FEATURE [PartDesign::Pad] Pad
  Direction = (1,-2e-16,3e-16)
  Length = 18.9
  Length2 = 10
  Placement = pos=(0,0,0) rot=(0.57735,0.57735,0.57735;2.0944rad)
  Profile = -> Sketch
  ReferenceAxis = -> Sketch [N_Axis]
  Type = 0
  expr: Length = <<Datasheet>>#<<mgn9c>>.Dim_L1
FEATURE [Sketcher::SketchObject] Sketch001
  ExternalGeometry = -> [Pad]
  FullyConstrained = true
  MapMode = 5
  Placement = pos=(-9e-16,-2,4e-16) rot=(-0.57735,-0.57735,0.57735;4.18879rad)
  Support = -> [Pad]
  expr: Constraints[10] = <<Datasheet>>#<<mgn9c>>.Dim_Wr + 2 mm
  sketch-geometry (4):
    g0: LineSegment StartX=-41 StartY=18.9 StartZ=0 EndX=-11 EndY=18.9 EndZ=0
    g1: LineSegment StartX=-11 StartY=18.9 StartZ=0 EndX=-11 EndY=11 EndZ=0
    g2: LineSegment StartX=-11 StartY=11 StartZ=0 EndX=-41 EndY=11 EndZ=0
    g3: LineSegment StartX=-41 StartY=11 StartZ=0 EndX=-41 EndY=18.9 EndZ=0
  constraints (11):
    c: Coincident(g0,g1)
    c: Coincident(g1,g2)
    c: Coincident(g2,g3)
    c: Coincident(g3,g0)
    c: Horizontal(g0)
    c: Horizontal(g2)
    c: Vertical(g1)
    c: Vertical(g3)
    c: Coincident(g0,g-4)
    c: PointOnObject(g1,g-3)
    c: DistanceY(g-3,g1) = 11
FEATURE [PartDesign::Pocket] Pocket
  BaseFeature = -> Pad
  Direction = (4e-16,1,-2e-16)
  Length = 5
  Length2 = 5
  Placement = pos=(0,0,0) rot=(0.57735,0.57735,0.57735;2.0944rad)
  Profile = -> Sketch001
  ReferenceAxis = -> Sketch001 [N_Axis]
  Type = 1
FEATURE [Sketcher::SketchObject] Sketch002
  ExternalGeometry = -> [Pocket]
  FullyConstrained = true
  MapMode = 5
  Placement = pos=(-1.15e-14,1.8e-14,41) rot=(0,0,-1;1.5708rad)
  Support = -> [Pocket]
  expr: Constraints[5] = <<Datasheet>>#<<mgn9c>>.Dim_H1 / 2 + <<Base>>#<<Sketch001>>.Constraints.PCB_Thickness
  expr: Constraints[7] = <<Datasheet>>#<<mgn9c>>.Dim_Wr
  sketch-geometry (9):
    g0: LineSegment StartX=-21 StartY=10 StartZ=0 EndX=-21 EndY=1 EndZ=0
    g1: LineSegment StartX=-21 StartY=1 StartZ=0 EndX=-24 EndY=1 EndZ=0
    g2: LineSegment StartX=-24 StartY=1 StartZ=0 EndX=-24 EndY=10 EndZ=0
    g3: GeomPoint X=-24 Y=5.5 Z=0
    g4: LineSegment StartX=-21 StartY=10 StartZ=0 EndX=-24 EndY=10 EndZ=0
    g5: LineSegment StartX=-24 StartY=1 StartZ=0 EndX=-21 EndY=1 EndZ=0
    g6: LineSegment StartX=-21 StartY=1 StartZ=0 EndX=-21 EndY=0 EndZ=0
    g7: LineSegment StartX=-21 StartY=0 StartZ=0 EndX=-24 EndY=0 EndZ=0
    g8: LineSegment StartX=-24 StartY=0 StartZ=0 EndX=-24 EndY=1 EndZ=0
  constraints (22):
    c: Coincident(g0,g1)
    c: Coincident(g1,g2)
    c: Horizontal(g1)
    c: Vertical(g0)
    c: Vertical(g2)
    c: DistanceX(g1,g1) = 3
    c: Symmetric(g2,g1,g3)
    c: DistanceY(g0,g0) = 9
    c: Horizontal(g4)
    c: Coincident(g5,g6)
    c: Coincident(g6,g7)
    c: Coincident(g7,g8)
    c: Coincident(g8,g5)
    c: Horizontal(g7)
    c: Vertical(g6)
    c: Vertical(g8)
    c: Coincident(g5,g1)
    c: PointOnObject(g6,g-1)
    c: Coincident(g0,g5)
    c: Coincident(g0,g4)
    c: Coincident(g2,g4)
    c: Symmetric(g-3,g7,g3)
FEATURE [PartDesign::Pocket] Pocket001
  BaseFeature = -> Pocket
  Direction = (7e-16,-7e-16,-1)
  Length = 5
  Length2 = 5
  Placement = pos=(0,0,0) rot=(0.57735,0.57735,0.57735;2.0944rad)
  Profile = -> Sketch002
  ReferenceAxis = -> Sketch002 [N_Axis]
  Type = 1
FEATURE [Sketcher::SketchObject] Sketch003
  ExternalGeometry = -> [Pocket001]
  FullyConstrained = true
  MapMode = 5
  Placement = pos=(9.2e-15,21,-1.41e-14) rot=(0.57735,0.57735,0.57735;4.18879rad)
  Support = -> [Pocket001]
  expr: Constraints[0] = <<Datasheet>>#<<mgn9c>>.Dim_d
  expr: Constraints[1] = <<Datasheet>>#<<mgn9c>>.Dim_d
  expr: Constraints[5] = <<Datasheet>>#<<mgn9c>>.Dim_E
  expr: Constraints[6] = <<Datasheet>>#<<mgn9c>>.Dim_P
  sketch-geometry (3):
    g0: Circle CenterX=13.5 CenterY=5.5 CenterZ=0 NormalX=0 NormalY=0 NormalZ=1 AngleXU=0 Radius=1.75
    g1: Circle CenterX=33.5 CenterY=5.5 CenterZ=0 NormalX=0 NormalY=0 NormalZ=1 AngleXU=0 Radius=1.75
    g2: LineSegment StartX=6 StartY=5.5 StartZ=0 EndX=33.5 EndY=5.5 EndZ=0
  constraints (8):
    c: Diameter(g1) = 3.5
    c: Diameter(g0) = 3.5
    c: Coincident(g2,g1)
    c: Horizontal(g2)
    c: PointOnObject(g0,g2)
    c: DistanceX(g2,g0) = 7.5
    c: DistanceX(g0,g1) = 20
    c: Symmetric(g-4,g-4,g2)
FEATURE [PartDesign::Pocket] Pocket002
  BaseFeature = -> Pocket001
  Direction = (-4e-16,-1,6e-16)
  Length = 5
  Length2 = 5
  Placement = pos=(0,0,0) rot=(0.57735,0.57735,0.57735;2.0944rad)
  Profile = -> Sketch003
  ReferenceAxis = -> Sketch003 [N_Axis]
  Type = 1
FEATURE [Sketcher::SketchObject] Sketch005
  ExternalGeometry = -> [Binder]
  FullyConstrained = true
  MapMode = 5
  Placement = pos=(-1e-14,6e-15,6) rot=(0.707107,0.707107,0;3.14159rad)
  sketch-geometry (3):
    g0: Circle CenterX=2.5 CenterY=14.45 CenterZ=0 NormalX=0 NormalY=0 NormalZ=1 AngleXU=0 Radius=1.5
    g1: Circle CenterX=17.5 CenterY=14.45 CenterZ=0 NormalX=0 NormalY=0 NormalZ=1 AngleXU=0 Radius=1.5
    g2: Circle CenterX=2.5 CenterY=4.45 CenterZ=0 NormalX=0 NormalY=0 NormalZ=1 AngleXU=0 Radius=1.5
  constraints (6):
    c: Coincident(g0,g-3)
    c: Tangent(g0,g-3)
    c: Coincident(g1,g-4)
    c: Tangent(g1,g-4)
    c: Coincident(g2,g-5)
    c: Tangent(g2,g-5)
FEATURE [PartDesign::Pocket] Pocket004
  BaseFeature = -> Pocket002
  Direction = (-1.7e-15,1e-15,1)
  Length = 5
  Length2 = 5
  Placement = pos=(0,0,0) rot=(0.57735,0.57735,0.57735;2.0944rad)
  Profile = -> Sketch005
  ReferenceAxis = -> Sketch005 [N_Axis]
  Type = 1
FEATURE [Sketcher::SketchObject] Sketch007
  ExternalGeometry = -> [Pocket004]
  FullyConstrained = true
  MapMode = 5
  Placement = pos=(-8e-16,1.2e-15,2.7564) rot=(0,0,-1;1.5708rad)
  Support = -> [Pocket004]
  expr: .Constraints.Rad = <<OmniballConnector_7945>>#<<Sketch002>>.Constraints.Smallest_Radius
  expr: Constraints[8] = .Constraints.Rad
  sketch-geometry (10):
    g0: LineSegment StartX=12.4944 StartY=18.9 StartZ=0 EndX=2 EndY=18.9 EndZ=0
    g1: LineSegment StartX=2 StartY=18.9 StartZ=0 EndX=2 EndY=5 EndZ=0
    g2: LineSegment StartX=2 StartY=5 StartZ=0 EndX=12.4944 EndY=5 EndZ=0
    g3: LineSegment StartX=12.4944 StartY=5 StartZ=0 EndX=12.4944 EndY=18.9 EndZ=0
    g4: Circle CenterX=8.9958 CenterY=2.5 CenterZ=0 NormalX=0 NormalY=0 NormalZ=1 AngleXU=0 Radius=1.2954
    g5: Circle CenterX=3.9986 CenterY=2.5 CenterZ=0 NormalX=0 NormalY=0 NormalZ=1 AngleXU=0 Radius=1.2954
    g6: GeomPoint X=3.9986 Y=5 Z=0
    g7: GeomPoint X=3.9986 Y=-4e-16 Z=0
    g8: GeomPoint X=7.4972 Y=2.5 Z=0
    g9: GeomPoint X=10.4944 Y=2.5 Z=0
  constraints (21):
    c: Coincident(g0,g1)
    c: Coincident(g1,g2)
    c: Coincident(g2,g3)
    c: Coincident(g3,g0)
    c: Horizontal(g2)
    c: Vertical(g1)
    c: Vertical(g3)
    c: Diameter(g4) = 2.5908  'Rad'
    c: Diameter(g5) = 2.5908
    c: Horizontal(g4,g5)
    c: Coincident(g0,g-5)
    c: PointOnObject(g6,g2)
    c: Symmetric(g6,g7,g5)
    c: Symmetric(g-6,g-7,g7)
    c: Vertical(g5,g7)
    c: DistanceY(g-4,g1) = 5
    c: PointOnObject(g8,g-8)
    c: PointOnObject(g9,g-3)
    c: Symmetric(g9,g8,g4)
    c: Horizontal(g4,g8)
    c: Coincident(g0,g-4)
FEATURE [PartDesign::Pocket] Pocket005
  BaseFeature = -> Pocket004
  Direction = (1.7e-15,-1e-15,-1)
  Length = 5
  Length2 = 5
  Placement = pos=(0,0,0) rot=(0.57735,0.57735,0.57735;2.0944rad)
  Profile = -> Sketch007
  ReferenceAxis = -> Sketch007 [N_Axis]
  Type = 1
FEATURE [PartDesign::SubShapeBinder] Binder002  label="OmniballConnector"
  BindCopyOnChange = 0
  BindMode = 0
  ClaimChildren = false
  Context = -> Body [Binder002.]
  Fuse = false
  MakeFace = true
  OffsetFill = false
  OffsetIntersection = false
  OffsetJoinType = 0
  OffsetOpenResult = false
  PartialLoad = false
  Placement = pos=(2.5,-4,2) rot=(0,1,0;3.14159rad)
  Relative = true
  Support = -> [<external OmniballConnector/OmniballConnector_7945.FCStd>#Body]
  _Version = 2
FEATURE [Sketcher::SketchObject] Sketch008
  ExternalGeometry = -> [Pocket005]
  FullyConstrained = true
  MapMode = 5
  Placement = pos=(-6e-16,9e-16,1.9944) rot=(0,0,-1;1.5708rad)
  Support = -> [Pocket005]
  sketch-geometry (2):
    g0: Circle CenterX=8.9958 CenterY=2.5 CenterZ=0 NormalX=0 NormalY=0 NormalZ=1 AngleXU=0 Radius=1.4986
    g1: Circle CenterX=3.9986 CenterY=2.5 CenterZ=0 NormalX=0 NormalY=0 NormalZ=1 AngleXU=0 Radius=1.4986
  constraints (4):
    c: Coincident(g0,g-3)
    c: Coincident(g1,g-5)
    c: Tangent(g1,g-7)
    c: Tangent(g0,g-4)
FEATURE [PartDesign::SubShapeBinder] Binder003  label="OmniballConnector2"
  BindCopyOnChange = 0
  BindMode = 0
  ClaimChildren = false
  Context = -> Body [Binder003.]
  Fuse = false
  MakeFace = true
  OffsetFill = false
  OffsetIntersection = false
  OffsetJoinType = 0
  OffsetOpenResult = false
  PartialLoad = false
  Placement = pos=(2.5,-9,2) rot=(0,1,0;3.14159rad)
  Relative = true
  Support = -> [<external OmniballConnector/OmniballConnector_7945.FCStd>#Body]
  _Version = 2
FEATURE [PartDesign::Pocket] Pocket006
  BaseFeature = -> Pocket005
  Direction = (3e-16,-4e-16,-1)
  Length = 0.762
  Length2 = 5
  Placement = pos=(0,0,0) rot=(0.57735,0.57735,0.57735;2.0944rad)
  Profile = -> Sketch008
  ReferenceAxis = -> Sketch008 [N_Axis]
  Type = 0
  expr: Length = 0.03 in
FEATURE [PartDesign::Body] Body  label="NormalConnector"
  Group = -> [Binder,Sketch,Binder001,Pad,Sketch001,Pocket,Sketch002,Pocket001,Sketch003,Pocket002,Sketch005,Pocket004,Sketch007,Pocket005,Binder002,Sketch008,Binder003,Pocket006]
  Origin = -> Origin
  Tip = -> Pocket006
COMPONENT P6 — same part as P1; its construction recipe is shown at P1.
COMPONENT P7 — geometry summary ("Rail"; no construction recipe available for this part):
  bounding box: 255.0 x 9.0 x 6.5 mm
  tessellated surface: 3,548 triangles
  volume: 14105 mm^3 (95% of its bounding box)
  symmetry: 2-fold rotationally symmetric about the x axis; 2-fold rotationally symmetric about the y axis; 2-fold rotationally symmetric about the z axis; mirror-symmetric across its x mid-plane, y mid-plane, z mid-plane
COMPONENT P8 — same part as P4; its construction recipe is shown at P4.
COMPONENT P9 — same part as P5; its construction recipe is shown at P5.
COMPONENT P10 — geometry summary ("Rail001"; no construction recipe available for this part):
  bounding box: 255.0 x 9.0 x 6.5 mm
  tessellated surface: 3,548 triangles
  volume: 14105 mm^3 (95% of its bounding box)
  symmetry: 2-fold rotationally symmetric about the x axis; 2-fold rotationally symmetric about the y axis; 2-fold rotationally symmetric about the z axis; mirror-symmetric across its x mid-plane, y mid-plane, z mid-plane
COMPONENT P11 — same part as P1; its construction recipe is shown at P1.
COMPONENT P12 — same part as P4; its construction recipe is shown at P4.
COMPONENT P13 — recipe-attached ("JoystickHolder", a linked part whose construction recipe lives in a companion FreeCAD document of the same project; that document's serialized recipe follows).
Construction recipe (the companion document, serialized — sketch geometry with constraints, then the solid features built on it; lengths are millimeters unless a unit is written):

FCSTD DOCUMENT  (FreeCAD 0.21R33668 +26 (Git))
Label: Joystick_Holder
License: All rights reserved
LicenseURL: http://en.wikipedia.org/wiki/All_rights_reserved
objects: Sketcher::SketchObject×6, PartDesign::Pad×4, PartDesign::SubShapeBinder×2, PartDesign::Pocket×2, PartDesign::Body×1
note: 21 computed .brp shape members not serialized (recipe doc carries the construction recipe); baked Part::Feature solids carry a one-line shape summary decoded from their .brp
EXTERNAL_REF file=MG/mgn9c_slide.FCStd obj=Body001
EXTERNAL_REF file=R202.FCStd obj=Revolution
EXTERNAL_REF file=MG/Datasheet.FCStd obj=Spreadsheet
EXTERNAL_REF file=NormalConnectorMagnet.FCStd obj=Sketch002
EXTERNAL_REF file=NormalConnectorMagnet.FCStd obj=Pad002
EXTERNAL_REF file=NormalConnectorMagnet.FCStd obj=Sketch003

FEATURE [PartDesign::SubShapeBinder] Binder  label="Slide"
  BindCopyOnChange = 0
  BindMode = 0
  ClaimChildren = false
  Context = -> Body [Binder.]
  Fuse = false
  MakeFace = true
  OffsetFill = false
  OffsetIntersection = false
  OffsetJoinType = 0
  OffsetOpenResult = false
  PartialLoad = false
  Placement = pos=(0,0,0) rot=(0,0,1;1.5708rad)
  Relative = true
  Support = -> [<external MG/mgn9c_slide.FCStd>#Body001]
  _Version = 2
FEATURE [PartDesign::SubShapeBinder] Binder001  label="Joystick"
  BindCopyOnChange = 0
  BindMode = 0
  ClaimChildren = false
  Context = -> Body [Binder001.]
  Fuse = false
  MakeFace = true
  OffsetFill = false
  OffsetIntersection = false
  OffsetJoinType = 0
  OffsetOpenResult = false
  PartialLoad = false
  Placement = pos=(-16.5,16.5,-29.5) rot=(0,0,-1;1.5708rad)
  Relative = true
  Support = -> [<external R202.FCStd>#Revolution]
  _Version = 2
FEATURE [Sketcher::SketchObject] Sketch
  ExternalGeometry = -> [Binder001]
  FullyConstrained = true
  MapMode = 5
  Placement = pos=(-16.5,16.5,0) rot=(0,0,-1;1.5708rad)
  Support = -> [Binder001]
  sketch-geometry (17):
    g0: LineSegment StartX=-20.2 StartY=25.2 StartZ=0 EndX=20.2 EndY=25.2 EndZ=0
    g1: LineSegment StartX=20.2 StartY=25.2 StartZ=0 EndX=20.2 EndY=20.2 EndZ=0
    g2: LineSegment StartX=20.2 StartY=20.2 StartZ=0 EndX=-20.2 EndY=20.2 EndZ=0
    g3: LineSegment StartX=-20.2 StartY=20.2 StartZ=0 EndX=-20.2 EndY=25.2 EndZ=0
    g4: LineSegment StartX=-20.2 StartY=20.2 StartZ=0 EndX=-20.2 EndY=-16.25 EndZ=0
    g5: LineSegment StartX=-12.3 StartY=-16.25 StartZ=0 EndX=-12.3 EndY=-12.4483 EndZ=0
    g6: ArcOfCircle CenterX=-16.25 CenterY=-16.25 CenterZ=0 NormalX=0 NormalY=0 NormalZ=1 AngleXU=0 Radius=3.95 StartAngle=3.14159 EndAngle=6.28319
    g7: ArcOfCircle CenterX=0 CenterY=-1.78e-14 CenterZ=0 NormalX=0 NormalY=0 NormalZ=1 AngleXU=0 Radius=17.5 StartAngle=5.4918 EndAngle=10.2162
    g8: LineSegment StartX=12.3 StartY=-12.4483 StartZ=0 EndX=12.3 EndY=-16.25 EndZ=0
    g9: ArcOfCircle CenterX=16.25 CenterY=-16.25 CenterZ=0 NormalX=0 NormalY=0 NormalZ=1 AngleXU=0 Radius=3.95 StartAngle=3.14159 EndAngle=6.28319
    g10: LineSegment StartX=20.2 StartY=20.2 StartZ=0 EndX=20.2 EndY=-16.25 EndZ=0
    g11: Circle CenterX=-16.25 CenterY=16.25 CenterZ=0 NormalX=0 NormalY=0 NormalZ=1 AngleXU=0 Radius=1
    g12: Circle CenterX=16.25 CenterY=16.25 CenterZ=0 NormalX=0 NormalY=0 NormalZ=1 AngleXU=0 Radius=1
    g13: Circle CenterX=16.25 CenterY=-16.25 CenterZ=0 NormalX=0 NormalY=0 NormalZ=1 AngleXU=0 Radius=1
    g14: Circle CenterX=-16.25 CenterY=-16.25 CenterZ=0 NormalX=0 NormalY=0 NormalZ=1 AngleXU=0 Radius=1
    g15: GeomPoint X=-16.25 Y=-17.25 Z=0
    g16: GeomPoint X=16.25 Y=-15.25 Z=0
  constraints (39):
    c: Coincident(g0,g1)
    c: Coincident(g1,g2)
    c: Coincident(g2,g3)
    c: Coincident(g3,g0)
    c: Horizontal(g0)
    c: Vertical(g1)
    c: Vertical(g3)
    c: Coincident(g1,g-8)
    c: Coincident(g2,g-8)
    c: DistanceY(g3,g3) = 5  'Strength'
    c: Coincident(g4,g3)
    c: Vertical(g4)
    c: PointOnObject(g5,g-9)
    c: Vertical(g5)
    c: Coincident(g6,g-5)
    c: Coincident(g6,g4)
    c: Horizontal(g4,g6)
    c: Tangent(g6,g5) = -1.5708
    c: Coincident(g7,g-9)
    c: Coincident(g7,g5)
    c: Coincident(g8,g7)
    c: Coincident(g9,g-6)
    c: Tangent(g9,g-7) = 1.5708
    c: Tangent(g9,g8) = -1.5708
    c: Horizontal(g8,g9)
    c: Coincident(g10,g1)
    c: Coincident(g10,g9)
    c: Coincident(g11,g-4)
    c: Tangent(g11,g-4)
    c: Coincident(g12,g-3)
    c: Tangent(g12,g-3)
    c: Coincident(g13,g9)
    c: Coincident(g14,g6)
    c: PointOnObject(g15,g-5)
    c: PointOnObject(g15,g14)
    c: PointOnObject(g16,g-6)
    c: PointOnObject(g16,g13)
    c: Vertical(g15,g6)
    c: Vertical(g16,g9)
FEATURE [PartDesign::Pad] Pad
  Direction = (0,0,1)
  Length = 3
  Length2 = 10
  Placement = pos=(-16.5,16.5,-29.5) rot=(0,0,-1;1.5708rad)
  Profile = -> Sketch
  ReferenceAxis = -> Sketch [N_Axis]
  Type = 0
FEATURE [Sketcher::SketchObject] Sketch001
  ExternalGeometry = -> [Pad]
  FullyConstrained = true
  MapMode = 5
  Placement = pos=(8.7,16.5,-29.5) rot=(0.57735,0.57735,0.57735;2.0944rad)
  Support = -> [Pad]
  expr: .Constraints.Rad = 3
  expr: Constraints[25] = .Constraints.Rad
  expr: Constraints[26] = .Constraints.Rad
  expr: Constraints[27] = .Constraints.Rad
  expr: Constraints[30] = <<Datasheet>>#<<mgn9c>>.Dim_C
  expr: Constraints[31] = <<Datasheet>>#<<mgn9c>>.Dim_B
  expr: Constraints[8] = <<Datasheet>>#<<mgn9c>>.Dim_L1
  expr: Constraints[9] = <<Datasheet>>#<<mgn9c>>.Dim_W
  sketch-geometry (14):
    g0: LineSegment StartX=-9.45 StartY=9.5 StartZ=0 EndX=9.45 EndY=9.5 EndZ=0
    g1: LineSegment StartX=9.45 StartY=9.5 StartZ=0 EndX=9.45 EndY=29.5 EndZ=0
    g2: LineSegment StartX=9.45 StartY=29.5 StartZ=0 EndX=-9.45 EndY=29.5 EndZ=0
    g3: LineSegment StartX=-9.45 StartY=29.5 StartZ=0 EndX=-9.45 EndY=9.5 EndZ=0
    g4: GeomPoint X=1.9e-15 Y=29.5 Z=0
    g5: Circle CenterX=-5 CenterY=27 CenterZ=0 NormalX=0 NormalY=0 NormalZ=1 AngleXU=0 Radius=1.5
    g6: Circle CenterX=5 CenterY=27 CenterZ=0 NormalX=0 NormalY=0 NormalZ=1 AngleXU=0 Radius=1.5
    g7: Circle CenterX=-5 CenterY=12 CenterZ=0 NormalX=0 NormalY=0 NormalZ=1 AngleXU=0 Radius=1.5
    g8: Circle CenterX=5 CenterY=12 CenterZ=0 NormalX=0 NormalY=0 NormalZ=1 AngleXU=0 Radius=1.5
    g9: LineSegment StartX=-5 StartY=12 StartZ=0 EndX=5 EndY=12 EndZ=0
    g10: LineSegment StartX=5 StartY=12 StartZ=0 EndX=5 EndY=27 EndZ=0
    g11: LineSegment StartX=5 StartY=27 StartZ=0 EndX=-5 EndY=27 EndZ=0
    g12: LineSegment StartX=-5 StartY=27 StartZ=0 EndX=-5 EndY=12 EndZ=0
    g13: GeomPoint X=1.8e-15 Y=19.5 Z=0
  constraints (32):
    c: Coincident(g0,g1)
    c: Coincident(g1,g2)
    c: Coincident(g2,g3)
    c: Coincident(g3,g0)
    c: Horizontal(g0)
    c: Horizontal(g2)
    c: Vertical(g1)
    c: Vertical(g3)
    c: DistanceX(g2,g2) = 18.9
    c: DistanceY(g1,g1) = 20
    c: Symmetric(g-3,g-4,g4)
    c: Symmetric(g2,g1,g4)
    c: Coincident(g9,g10)
    c: Coincident(g10,g11)
    c: Coincident(g11,g12)
    c: Coincident(g12,g9)
    c: Horizontal(g9)
    c: Horizontal(g11)
    c: Vertical(g10)
    c: Vertical(g12)
    c: Coincident(g9,g7)
    c: Coincident(g10,g6)
    c: Coincident(g5,g11)
    c: Coincident(g8,g9)
    c: Diameter(g7) = 3  'Rad'
    c: Diameter(g8) = 3
    c: Diameter(g6) = 3
    c: Diameter(g5) = 3
    c: Symmetric(g1,g0,g13)
    c: Symmetric(g7,g6,g13)
    c: DistanceX(g11,g11) = 10
    c: DistanceY(g10,g10) = 15
FEATURE [PartDesign::Pad] Pad001
  BaseFeature = -> Pad
  Direction = (1,4e-16,0)
  Length = 5
  Length2 = 10
  Placement = pos=(-16.5,16.5,-29.5) rot=(0,0,-1;1.5708rad)
  Profile = -> Sketch001
  ReferenceAxis = -> Sketch001 [N_Axis]
  Reversed = true
  Type = 0
  expr: Length = <<Sketch>>.Constraints.Strength
FEATURE [Sketcher::SketchObject] Sketch002
  ExternalGeometry = -> [Pad001]
  FullyConstrained = true
  MapMode = 5
  Placement = pos=(3.7,16.5,-29.5) rot=(0.57735,-0.57735,-0.57735;2.0944rad)
  Support = -> [Pad001]
  sketch-geometry (4):
    g0: LineSegment StartX=-9.45 StartY=9.5 StartZ=0 EndX=-7.45 EndY=9.5 EndZ=0
    g1: LineSegment StartX=-7.45 StartY=9.5 StartZ=0 EndX=-7.45 EndY=7.5 EndZ=0
    g2: LineSegment StartX=-7.45 StartY=7.5 StartZ=0 EndX=-9.45 EndY=7.5 EndZ=0
    g3: LineSegment StartX=-9.45 StartY=7.5 StartZ=0 EndX=-9.45 EndY=9.5 EndZ=0
  constraints (11):
    c: Coincident(g0,g1)
    c: Coincident(g1,g2)
    c: Coincident(g2,g3)
    c: Coincident(g3,g0)
    c: Horizontal(g0)
    c: Horizontal(g2)
    c: Vertical(g1)
    c: Vertical(g3)
    c: DistanceX(g2,g2) = 2
    c: Coincident(g0,g-3)
    c: DistanceY(g1,g1) = 2
FEATURE [PartDesign::Pad] Pad002
  BaseFeature = -> Pad001
  Direction = (-1,-4e-16,0)
  Length = 13
  Length2 = 10
  Placement = pos=(-16.5,16.5,-29.5) rot=(0,0,-1;1.5708rad)
  Profile = -> Sketch002
  ReferenceAxis = -> Sketch002 [N_Axis]
  Reversed = true
  Type = 0
  expr: Length = <<Pad001>>.Length + <<Datasheet>>#<<mgn9c>>.Dim_H - <<Datasheet>>#<<mgn9c>>.Dim_H1
FEATURE [Sketcher::SketchObject] Sketch003
  ExternalGeometry = -> [Pad002]
  FullyConstrained = true
  MapMode = 5
  Placement = pos=(16.7,16.5,-29.5) rot=(0.57735,0.57735,0.57735;2.0944rad)
  Support = -> [Pad002]
  expr: Constraints[17] = <<NormalConnectorMagnet>>#<<Sketch002>>.Constraints.SlideToMagnetCenter
  sketch-geometry (13):
    g0: LineSegment StartX=9.45 StartY=9.5 StartZ=0 EndX=4.45 EndY=9.5 EndZ=0
    g1: LineSegment StartX=4.45 StartY=9.5 StartZ=0 EndX=4.45 EndY=2.35 EndZ=0
    g2: LineSegment StartX=4.45 StartY=2.35 StartZ=0 EndX=9.45 EndY=2.35 EndZ=0
    g3: LineSegment StartX=9.45 StartY=2.35 StartZ=0 EndX=9.45 EndY=9.5 EndZ=0
    g4: Circle CenterX=6.95 CenterY=4.85 CenterZ=0 NormalX=0 NormalY=0 NormalZ=1 AngleXU=0 Radius=1.5
    g5: GeomPoint X=8.45 Y=4.85 Z=0
    g6: GeomPoint X=6.95 Y=3.35 Z=0
    g7: LineSegment StartX=6.95 StartY=3.35 StartZ=0 EndX=6.95 EndY=2.35 EndZ=0
    g8: LineSegment StartX=7.45 StartY=7.5 StartZ=0 EndX=4.45 EndY=6.35 EndZ=0
    g9: LineSegment StartX=4.45 StartY=6.35 StartZ=0 EndX=4.45 EndY=2.35 EndZ=0
    g10: GeomPoint X=6.95 Y=6.35 Z=0
    g11: LineSegment StartX=7.45 StartY=9.5 StartZ=0 EndX=9.45 EndY=9.5 EndZ=0
    g12: LineSegment StartX=7.45 StartY=7.5 StartZ=0 EndX=7.45 EndY=9.5 EndZ=0
  constraints (32):
    c: Coincident(g0,g1)
    c: Coincident(g1,g2)
    c: Coincident(g2,g3)
    c: Coincident(g3,g0)
    c: Horizontal(g0)
    c: Horizontal(g2)
    c: Vertical(g1)
    c: Vertical(g3)
    c: PointOnObject(g-3,g3)
    c: PointOnObject(g-4,g0)
    c: Diameter(g4) = 3
    c: PointOnObject(g5,g4)
    c: DistanceX(g5,g0) = 1
    c: PointOnObject(g6,g4)
    c: DistanceY(g2,g6) = 1
    c: Horizontal(g5,g4)
    c: Vertical(g4,g6)
    c: DistanceY(g4,g0) = 4.65
    c: Coincident(g7,g6)
    c: Vertical(g7)
    c: Symmetric(g1,g2,g7)
    c: Coincident(g8,g-4)
    c: PointOnObject(g8,g1)
    c: Coincident(g9,g8)
    c: Coincident(g9,g2)
    c: PointOnObject(g10,g4)
    c: Vertical(g10,g4)
    c: Horizontal(g8,g10)
    c: Coincident(g12,g11)
    c: Coincident(g11,g-4)
    c: Coincident(g0,g11)
    c: Coincident(g8,g12)
FEATURE [PartDesign::Pad] Pad003
  BaseFeature = -> Pad002
  Direction = (1,4e-16,0)
  Length = 2
  Length2 = 10
  Placement = pos=(-16.5,16.5,-29.5) rot=(0,0,-1;1.5708rad)
  Profile = -> Sketch003
  ReferenceAxis = -> Sketch003 [N_Axis]
  Reversed = true
  Type = 0
  expr: Length = <<NormalConnectorMagnet>>#<<Pad002>>.Length
FEATURE [Sketcher::SketchObject] Sketch004
  ExternalGeometry = -> [Pad003]
  FullyConstrained = true
  MapMode = 5
  Placement = pos=(14.7,16.5,-29.5) rot=(0.57735,-0.57735,-0.57735;2.0944rad)
  Support = -> [Pad003]
  expr: Constraints[1] = <<NormalConnectorMagnet>>#<<Sketch003>>.Constraints.MagnetDiameter
  sketch-geometry (1):
    g0: Circle CenterX=-6.95 CenterY=4.85 CenterZ=0 NormalX=0 NormalY=0 NormalZ=1 AngleXU=0 Radius=2
  constraints (2):
    c: Coincident(g0,g-3)
    c: Diameter(g0) = 4
FEATURE [PartDesign::Pocket] Pocket
  BaseFeature = -> Pad003
  Direction = (1,0,0)
  Length = 1
  Length2 = 5
  Placement = pos=(-16.5,16.5,-29.5) rot=(0,0,-1;1.5708rad)
  Profile = -> Sketch004
  ReferenceAxis = -> Sketch004 [N_Axis]
  Type = 0
FEATURE [Sketcher::SketchObject] Sketch005
  ExternalGeometry = -> [Pocket]
  FullyConstrained = true
  MapMode = 5
  Placement = pos=(3.7,16.5,-29.5) rot=(0.57735,-0.57735,-0.57735;2.0944rad)
  Support = -> [Pocket]
  expr: Constraints[1] = <<Datasheet>>#<<mgn9c>>.Dim_D
  expr: Constraints[5] = <<Datasheet>>#<<mgn9c>>.Dim_D
  expr: Constraints[6] = <<Datasheet>>#<<mgn9c>>.Dim_D
  expr: Constraints[7] = <<Datasheet>>#<<mgn9c>>.Dim_D
  sketch-geometry (14):
    g0: Circle CenterX=-5 CenterY=27 CenterZ=0 NormalX=0 NormalY=0 NormalZ=1 AngleXU=0 Radius=3
    g1: Circle CenterX=5 CenterY=27 CenterZ=0 NormalX=0 NormalY=0 NormalZ=1 AngleXU=0 Radius=3
    g2: Circle CenterX=5 CenterY=12 CenterZ=0 NormalX=0 NormalY=0 NormalZ=1 AngleXU=0 Radius=3
    g3: Circle CenterX=-5 CenterY=12 CenterZ=0 NormalX=0 NormalY=0 NormalZ=1 AngleXU=0 Radius=3
    g4: ArcOfCircle CenterX=-5 CenterY=12 CenterZ=0 NormalX=0 NormalY=0 NormalZ=1 AngleXU=0 Radius=3 StartAngle=2.26252e-07 EndAngle=3.14159
    g5: ArcOfCircle CenterX=5 CenterY=12 CenterZ=0 NormalX=0 NormalY=0 NormalZ=1 AngleXU=0 Radius=3 StartAngle=6.28318 EndAngle=9.42479
    g6: LineSegment StartX=2 StartY=9.5 StartZ=0 EndX=8 EndY=9.5 EndZ=0
    g7: LineSegment StartX=8 StartY=9.5 StartZ=0 EndX=8 EndY=12 EndZ=0
    g8: LineSegment StartX=8 StartY=12 StartZ=0 EndX=2 EndY=12 EndZ=0
    g9: LineSegment StartX=2 StartY=12 StartZ=0 EndX=2 EndY=9.5 EndZ=0
    g10: LineSegment StartX=-2 StartY=7.5 StartZ=0 EndX=-8 EndY=7.5 EndZ=0
    g11: LineSegment StartX=-8 StartY=7.5 StartZ=0 EndX=-8 EndY=12 EndZ=0
    g12: LineSegment StartX=-8 StartY=12 StartZ=0 EndX=-2 EndY=12 EndZ=0
    g13: LineSegment StartX=-2 StartY=12 StartZ=0 EndX=-2 EndY=7.5 EndZ=0
  constraints (36):
    c: Coincident(g0,g-3)
    c: Diameter(g0) = 6
    c: Coincident(g1,g-4)
    c: Coincident(g2,g-5)
    c: Coincident(g3,g-6)
    c: Diameter(g1) = 6
    c: Diameter(g2) = 6
    c: Diameter(g3) = 6
    c: Coincident(g4,g3)
    c: PointOnObject(g4,g3)
    c: Coincident(g5,g2)
    c: PointOnObject(g5,g2)
    c: Coincident(g6,g7)
    c: Coincident(g7,g8)
    c: Coincident(g8,g9)
    c: Coincident(g9,g6)
    c: Horizontal(g6)
    c: Horizontal(g8)
    c: Vertical(g7)
    c: Vertical(g9)
    c: Coincident(g7,g5)
    c: PointOnObject(g6,g-7)
    c: Coincident(g5,g8)
    c: Coincident(g10,g11)
    c: Coincident(g11,g12)
    c: Coincident(g12,g13)
    c: Coincident(g13,g10)
    c: Horizontal(g10)
    c: Horizontal(g12)
    c: Vertical(g11)
    c: Vertical(g13)
    c: Coincident(g11,g4)
    c: Coincident(g4,g12)
    c: Tangent(g13,g4)
    c: Tangent(g9,g5)
    c: PointOnObject(g-8,g10)
FEATURE [PartDesign::Pocket] Pocket001
  BaseFeature = -> Pocket
  Direction = (1,9e-16,0)
  Length = 3
  Length2 = 5
  Placement = pos=(-16.5,16.5,-29.5) rot=(0,0,-1;1.5708rad)
  Profile = -> Sketch005
  ReferenceAxis = -> Sketch005 [N_Axis]
  Type = 4
  expr: Length = <<Pad001>>.Length - 2 mm
FEATURE [PartDesign::Body] Body  label="JoystickHolder"
  Group = -> [Binder,Binder001,Sketch,Pad,Sketch001,Pad001,Sketch002,Pad002,Sketch003,Pad003,Sketch004,Pocket,Sketch005,Pocket001]
  Origin = -> Origin
  Placement = pos=(0,0,-4) rot=(0,0,1;0rad)
  Tip = -> Pocket001
PROVENANCE & LICENSES
A FreeCAD (.FCStd) document from a public repository crawl; recipes are the document's own serialized feature recipes (and, for linked parts, companion documents' recipes).
License: as declared in the source repository (recorded in the dataset sidecar).
